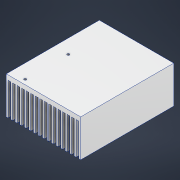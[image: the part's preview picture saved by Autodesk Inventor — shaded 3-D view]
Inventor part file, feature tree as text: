
AUTODESK INVENTOR PART (.ipt)
format: ipt  version: 2022 (Build 260153000, 153)  size: 187,392 bytes
history: native  units: in
note: dims shown in document units (in); Inventor stores cm internally (conversion verified against a paired STEP export)
features: sketch x2, extrude x1, hole x1
ambient origin geometry x8: Origin, YZ Plane, XZ Plane, XY Plane, X Axis, Y Axis, Z Axis, Center Point
bodies: Solid1 (feature_tree)
feature tree (4):
  extrude  "Extrusion1"  Depth=3.1496in
  hole  "Hole1"  [1 undecoded]
  sketch  "Sketch1"  dims[d0=1.5748in d1=3.1496in]
  sketch  "Sketch2"  dims[d2=0.0787in d3=0.1969in d4=6.2992in d6=0.1919in d7=0.3937in d9=1.0in d11=0.0787in d12=0.0787in d13=3.937in d14=0.0in d15=1.82in d17=0.6in d18=0.203in d19=0.0968in d20=0.236in d21=0.375in d22=0.25in d23=0.5635in d24=1.0in d25=0.8108in]
note: 1 required parameter value undecoded (feature->parameter linkage not recoverable at this tier; creation-order binding heuristic only, values carry confidence <= 0.55)
